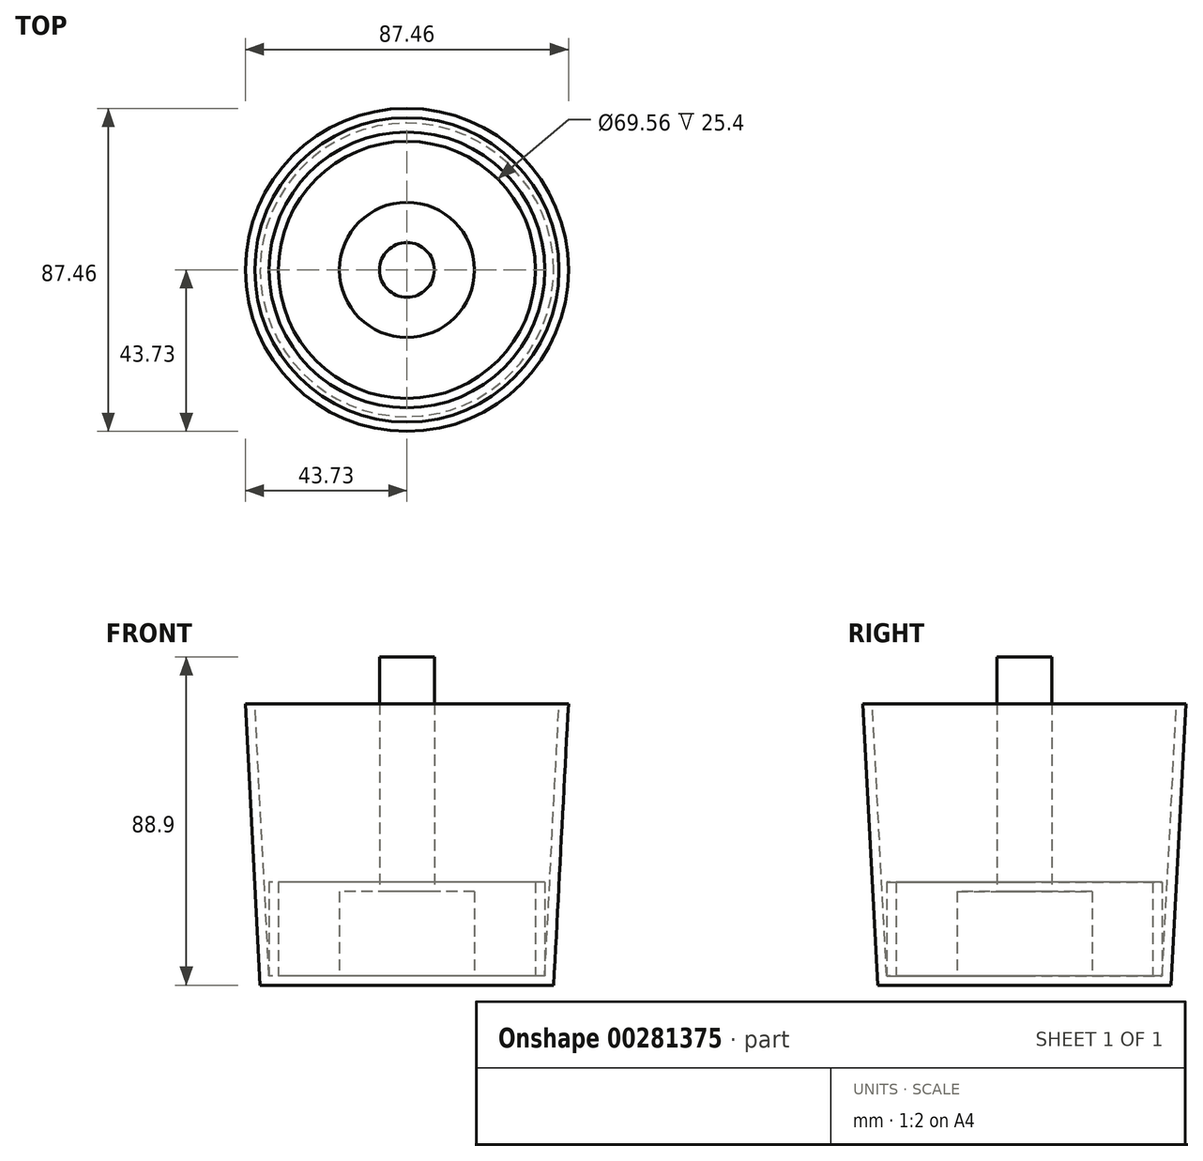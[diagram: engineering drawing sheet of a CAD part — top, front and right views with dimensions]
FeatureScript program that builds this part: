
annotation { "Feature Type Name" : "Feature", "Feature Type Description" : "" }
export const myFeature = defineFeature(function(context is Context, id is Id, definition is map)
    precondition{}
    {
        {
            var Q0;
            Q0=qCreatedBy(makeId("Top.planeOp"),FACE);
            var sketch = newSketch(context, id + "F0", { "sketchPlane" : qUnion([Q0])});
            skCircle(sketch, "E0", {"center": v(0, 0) * mm, "radius": 39.73 * mm});
            skSolve(sketch);
        }
        {
            var Q0;
            Q0=makeQuery(id+"F0.imprint","IMPRINT",FACE,{"disambiguationData":[TD([[makeQuery(id+"F0.imprint","IMPRINT",EDGE,{"derivedFrom":sQuery(id+"F0.wireOp",EDGE,"E0")}),1.0]])]});
            extrude(context, id + "F1", {"entities" : qUnion([Q0]), "depth" : 76.2 * mm, "hasDraft" : true, "draftAngle" : 3 * degree});
        }
        {
            var Q0;
            Q0=makeQuery(id+"F1.opExtrude","CAP_FACE",FACE,{"disambiguationData":[OSD([sQuery(id+"F0.wireOp",EDGE,"E0")])],"isStart":false});
            shell(context, id + "F2", {"entities" : qUnion([Q0]), "thickness" : 2.54 * mm});
        }
        {
            var Q0;
            {var subQ0=sQuery(id+"F0.wireOp",EDGE,"E0");Q0=makeQuery(id+"F2.opShell","OFFSET_FACE",FACE,{"disambiguationData":[OSD([subQ0]),TDD([makeQuery(id+"F1.opExtrude","CAP_FACE",FACE,{"disambiguationData":[OSD([subQ0])],"isStart":true})])]});}
            extrude(context, id + "F3", {"entities" : qUnion([Q0]), "operationType" : NewBodyOperationType.ADD, "depth" : 25.4 * mm});
        }
        {
            var Q0;
            Q0=makeQuery(id+"F3.opExtrude","CAP_FACE",FACE,{"disambiguationData":[OSD([sQuery(id+"F0.wireOp",EDGE,"E0")])],"isStart":false});
            shell(context, id + "F4", {"entities" : qUnion([Q0]), "thickness" : 2.54 * mm});
        }
        {
            var Q0;
            Q0=qCreatedBy(makeId("Top.planeOp"),FACE);
            var sketch = newSketch(context, id + "F5", { "sketchPlane" : qUnion([Q0])});
            skCircle(sketch, "E1", {"center": v(0, 0) * mm, "radius": 18.28 * mm});
            skSolve(sketch);
        }
        {
            var Q0;
            Q0 = qSketchRegion(id + "F5", true);
            extrude(context, id + "F6", {"entities" : qUnion([Q0]), "operationType" : NewBodyOperationType.ADD, "depth" : 25.4 * mm});
        }
        {
            var Q0;
            Q0=qCreatedBy(makeId("Top.planeOp"),FACE);
            var sketch = newSketch(context, id + "F7", { "sketchPlane" : qUnion([Q0])});
            skCircle(sketch, "E2", {"center": v(0, 0) * mm, "radius": 7.41 * mm});
            skSolve(sketch);
        }
        {
            var Q0;
            Q0 = qSketchRegion(id + "F7", true);
            extrude(context, id + "F8", {"entities" : qUnion([Q0]), "operationType" : NewBodyOperationType.ADD, "depth" : 88.9 * mm});
        }
    });
